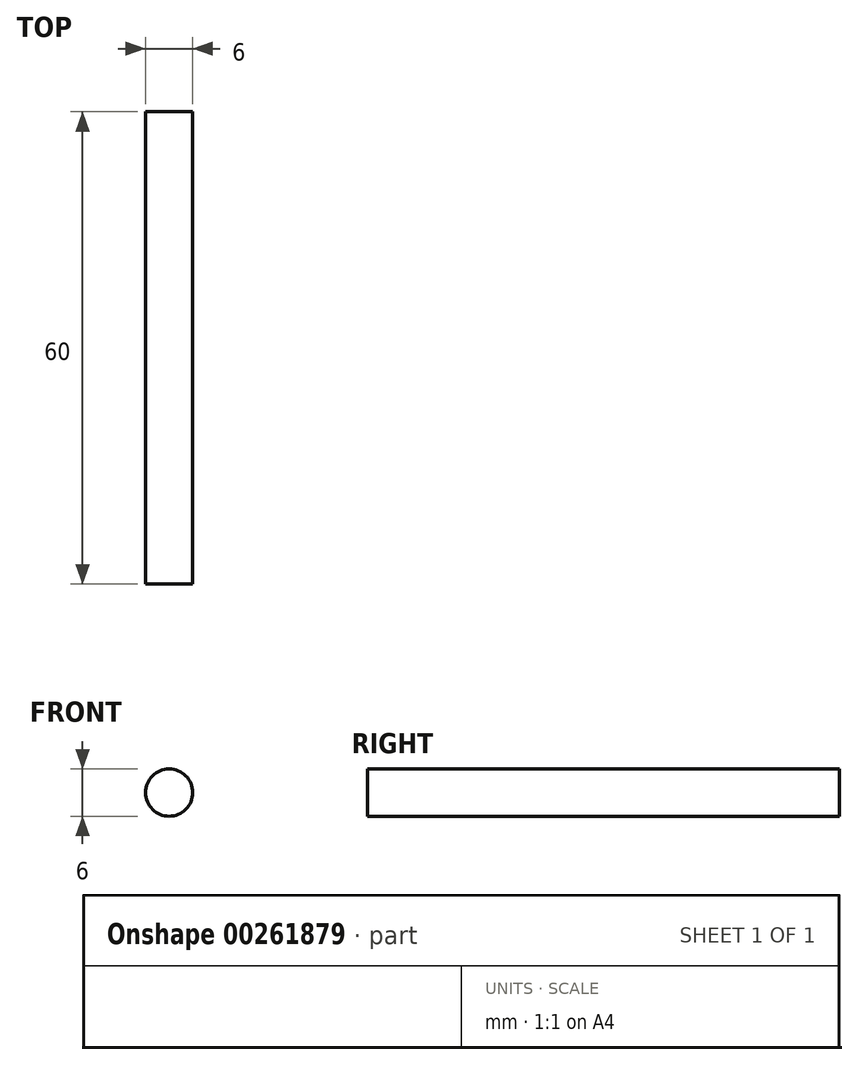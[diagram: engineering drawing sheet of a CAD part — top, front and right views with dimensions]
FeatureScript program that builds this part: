
annotation { "Feature Type Name" : "Feature", "Feature Type Description" : "" }
export const myFeature = defineFeature(function(context is Context, id is Id, definition is map)
    precondition{}
    {
        {
            var Q0;
            Q0=qCreatedBy(makeId("Front.planeOp"),FACE);
            var sketch = newSketch(context, id + "F0", { "sketchPlane" : qUnion([Q0])});
            skCircle(sketch, "E0", {"center": v(0, 0) * mm, "radius": 3 * mm});
            skSolve(sketch);
        }
        {
            var Q0;
            Q0=makeQuery(id+"F0.imprint","IMPRINT",FACE,{"disambiguationData":[TD([[makeQuery(id+"F0.imprint","IMPRINT",EDGE,{"derivedFrom":sQuery(id+"F0.wireOp",EDGE,"E0")}),1.0]])]});
            extrude(context, id + "F1", {"entities" : qUnion([Q0]), "endBound" : BoundingType.SYMMETRIC, "depth" : 60 * mm});
        }
    });
